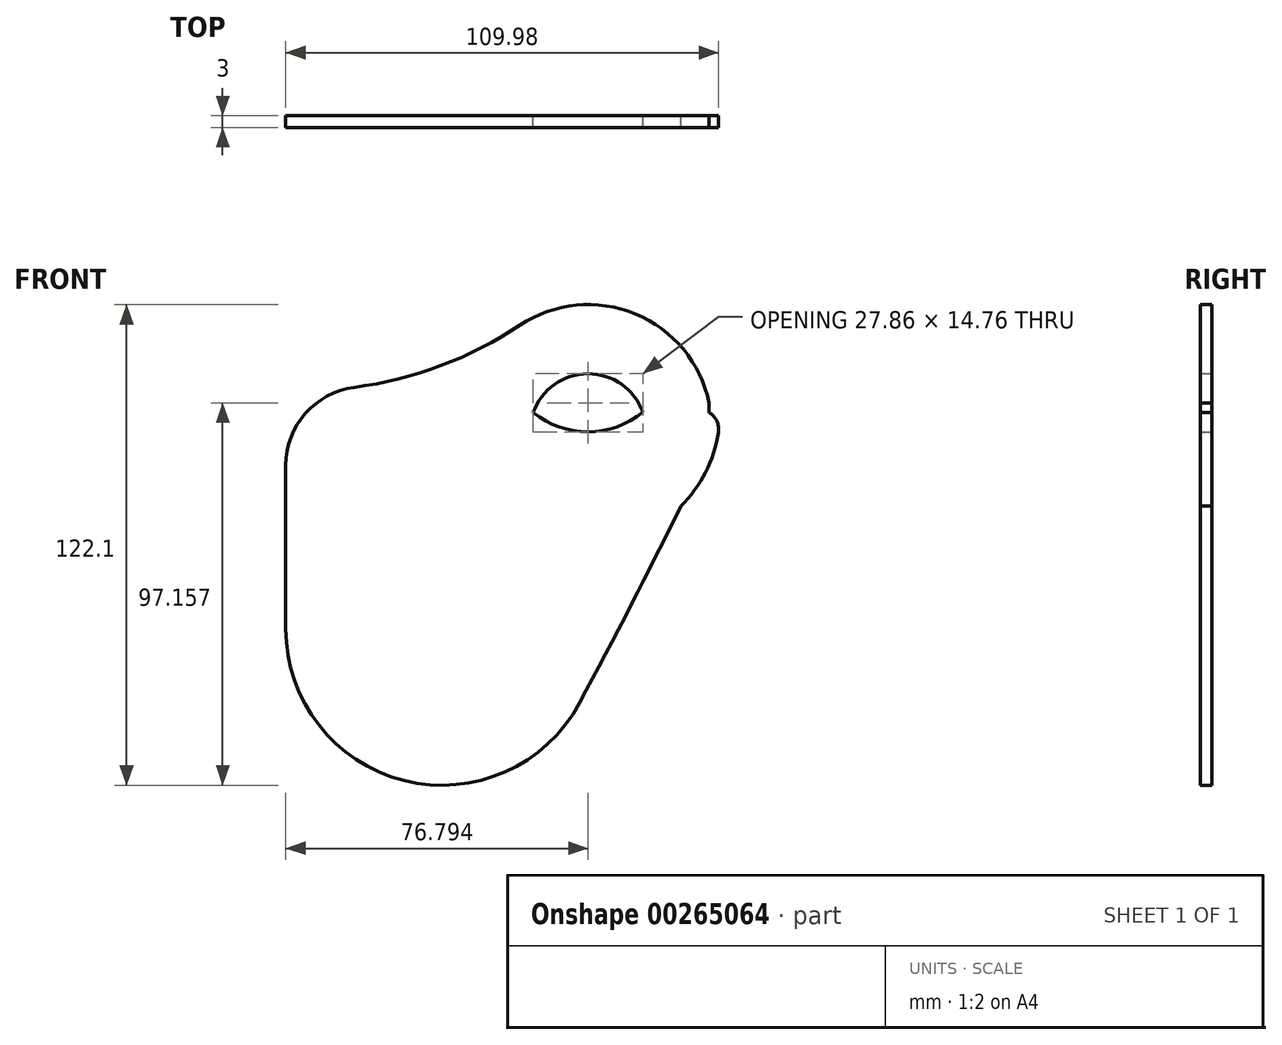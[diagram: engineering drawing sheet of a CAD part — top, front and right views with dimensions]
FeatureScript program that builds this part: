
annotation { "Feature Type Name" : "Feature", "Feature Type Description" : "" }
export const myFeature = defineFeature(function(context is Context, id is Id, definition is map)
    precondition{}
    {
        {
            var Q0;
            Q0=qCreatedBy(makeId("Front.planeOp"),FACE);
            var sketch = newSketch(context, id + "F0", { "sketchPlane" : qUnion([Q0])});
            skArc(sketch, "E0", {"start": v(-23.37, 71.6) * mm, "mid": v(-42.37, 87.06) * mm, "end": v(-61.37, 71.6) * mm});
            skPoint(sketch, "E1", {"position": v(-25.38, 77.03) * mm});
            skArc(sketch, "E2", {"start": v(-56.37, 71.6) * mm, "mid": v(-42.42, 66.69) * mm, "end": v(-28.5, 71.7) * mm});
            skArc(sketch, "E3", {"start": v(-28.5, 71.7) * mm, "mid": v(-42.48, 81.45) * mm, "end": v(-56.37, 71.6) * mm});
            skPoint(sketch, "E4", {"position": v(-42.37, 87.06) * mm});
            skPoint(sketch, "E5", {"position": v(-30.58, 56.7) * mm});
            skArc(sketch, "E6", {"start": v(-61.37, 71.6) * mm, "mid": v(-42.37, 52.6) * mm, "end": v(-23.37, 71.6) * mm});
            skPoint(sketch, "E7", {"position": v(-42.37, 52.6) * mm});
            skPoint(sketch, "E8", {"position": v(-61.37, 71.6) * mm});
            skPoint(sketch, "E9", {"position": v(-56.96, 80.44) * mm});
            skPoint(sketch, "E10", {"position": v(-68.92, 94.73) * mm});
            skArc(sketch, "E11", {"start": v(-57.31, 4.66) * mm, "mid": v(-44.8, 28.42) * mm, "end": v(-32.7, 52.4) * mm});
            skPoint(sketch, "E12", {"position": v(-29.37, 71.03) * mm});
            skLineSegment(sketch, "E13", {"start": v(-104.78, 66.2) * mm, "end": v(-104.78, 16.6) * mm});
            skArc(sketch, "E14", {"start": v(-104.78, 16.6) * mm, "mid": v(-85.7, -7.88) * mm, "end": v(-57.31, 4.66) * mm});
            skPoint(sketch, "E15", {"position": v(-85.15, 92.16) * mm});
            skPoint(sketch, "E16", {"position": v(-79.37, -8.64) * mm});
            skPoint(sketch, "E17.endSnap0", {"position": v(-42.4, 59.62) * mm});
            skLineSegment(sketch, "E18", {"start": v(-28.5, 71.7) * mm, "end": v(-23.37, 71.6) * mm});
            skLineSegment(sketch, "E19", {"start": v(-61.37, 71.6) * mm, "end": v(-56.37, 71.6) * mm});
            skLineSegment(sketch, "E20", {"start": v(-42.42, 66.69) * mm, "end": v(-42.42, 66.65) * mm});
            skPoint(sketch, "E21", {"position": v(-24.15, 66.23) * mm});
            skPoint(sketch, "E22", {"position": v(-59.84, 76.1) * mm});
            skPoint(sketch, "E23", {"position": v(-60.59, 66.2) * mm});
            skLineSegment(sketch, "E24.bottom", {"start": v(-26.7, 79.1) * mm, "end": v(-27.38, 79.1) * mm});
            skPoint(sketch, "E25", {"position": v(-108.66, 79.1) * mm});
            skLineSegment(sketch, "E26.top", {"start": v(-109.39, 67.1) * mm, "end": v(-109.78, 67.1) * mm});
            skLineSegment(sketch, "E27.left", {"start": v(-39.95, 71.09) * mm, "end": v(-39.95, 71.09) * mm});
            skLineSegment(sketch, "E27.right", {"start": v(-42.68, 71.09) * mm, "end": v(-42.68, 71.09) * mm});
            skLineSegment(sketch, "E28.top", {"start": v(-63.18, 66.2) * mm, "end": v(-68.59, 66.2) * mm});
            skPoint(sketch, "E29.orphan", {"position": v(-114.78, 67.1) * mm});
            skPoint(sketch, "E30.top.start.orphan", {"position": v(-109.78, 64.1) * mm});
            skPoint(sketch, "E17.end.orphan", {"position": v(-42.4, 81.45) * mm});
            skLineSegment(sketch, "E31.trimOffspring", {"start": v(-109.78, 54.6) * mm, "end": v(-109.78, 51.6) * mm});
            skPoint(sketch, "E32.top.end.orphan", {"position": v(-106.78, 10.37) * mm});
            skPoint(sketch, "E32.left.start.orphan", {"position": v(-109.78, 35.77) * mm});
            skPoint(sketch, "E27.bottom.start.orphan", {"position": v(-48.6, 10.37) * mm});
            skPoint(sketch, "E27.top.end.orphan", {"position": v(-51.33, 10.37) * mm});
            skPoint(sketch, "E33.start.orphan", {"position": v(-38.82, 35.77) * mm});
            skArc(sketch, "E34.0", {"start": v(-55.1, 3.47) * mm, "mid": v(-41.61, 29.17) * mm, "end": v(-28.58, 55.1) * mm});
            skArc(sketch, "E34.1", {"start": v(-107.28, 16.6) * mm, "mid": v(-86.31, -10.3) * mm, "end": v(-55.1, 3.47) * mm});
            skLineSegment(sketch, "E34.2", {"start": v(-107.28, 66.2) * mm, "end": v(-107.28, 16.6) * mm});
            skLineSegment(sketch, "E35", {"start": v(-20.87, 71.6) * mm, "end": v(-23.37, 71.6) * mm});
            skLineSegment(sketch, "E36", {"start": v(-68.59, 66.2) * mm, "end": v(-107.28, 66.2) * mm});
            skArc(sketch, "E37.0", {"start": v(-63.87, 71.6) * mm, "mid": v(-42.37, 50.1) * mm, "end": v(-20.87, 71.6) * mm});
            skLineSegment(sketch, "E38", {"start": v(-61.37, 71.6) * mm, "end": v(-63.87, 71.6) * mm});
            skPoint(sketch, "E39", {"position": v(-80.6, -11.12) * mm});
            skPoint(sketch, "E40", {"position": v(-80.6, 66.2) * mm});
            skArc(sketch, "E41.0", {"start": v(-44.59, -2.18) * mm, "mid": v(-31.5, 22.7) * mm, "end": v(-18.85, 47.82) * mm});
            skArc(sketch, "E41.1", {"start": v(-119.23, 16.6) * mm, "mid": v(-89.23, -21.89) * mm, "end": v(-44.59, -2.18) * mm});
            skLineSegment(sketch, "E41.2", {"start": v(-119.23, 66.2) * mm, "end": v(-119.23, 16.6) * mm});
            skArc(sketch, "E42.0", {"start": v(-11.67, 74.02) * mm, "mid": v(-40.22, 98.93) * mm, "end": v(-71.9, 78.15) * mm});
            skLineSegment(sketch, "E43.0", {"start": v(-71.9, 78.15) * mm, "end": v(-107.28, 78.15) * mm});
            skArc(sketch, "E44.0", {"start": v(-18.85, 47.82) * mm, "mid": v(-11.5, 58.71) * mm, "end": v(-8.93, 71.6) * mm});
            skLineSegment(sketch, "E45", {"start": v(-119.23, 66.2) * mm, "end": v(-119.23, 78.15) * mm});
            skLineSegment(sketch, "E46", {"start": v(-107.28, 78.15) * mm, "end": v(-119.23, 78.15) * mm});
            skLineSegment(sketch, "E47", {"start": v(-8.93, 71.6) * mm, "end": v(-11.67, 71.6) * mm});
            skLineSegment(sketch, "E48", {"start": v(-11.67, 71.6) * mm, "end": v(-11.67, 74.02) * mm});
            skPoint(sketch, "E49.orphan", {"position": v(-73.06, 74.02) * mm});
            skPoint(sketch, "E50.end.orphan", {"position": v(-73.06, 71.6) * mm});
            skPoint(sketch, "E51.orphan", {"position": v(-119.23, 79.1) * mm});
            skLineSegment(sketch, "E52", {"start": v(-8.93, 71.6) * mm, "end": v(-14.38, 81.77) * mm});
            skSolve(sketch);
        }
        {
            var Q0;
            Q0=makeQuery(id+"F0.imprint","IMPRINT",FACE,{"disambiguationData":[TD([[makeQuery(id+"F0.imprint","IMPRINT",EDGE,{"derivedFrom":sQuery(id+"F0.wireOp",EDGE,"E3")}),-1.0]])]});
            var Q1;
            {var subQ2=sQuery(id+"F0.wireOp",EDGE,"E11");Q1=makeQuery(id+"F0.imprint","IMPRINT",FACE,{"disambiguationData":[TD([[makeQuery(id+"F0.imprint","IMPRINT",EDGE,{"derivedFrom":subQ2}),-1.0]])]});}
            var Q2;
            Q2=makeQuery(id+"F0.imprint","IMPRINT",FACE,{"disambiguationData":[TD([[makeQuery(id+"F0.imprint","IMPRINT",EDGE,{"derivedFrom":sQuery(id+"F0.wireOp",EDGE,"E6")}),1.0]])]});
            var Q3;
            {var subQ1=sQuery(id+"F0.wireOp",EDGE,"E11");Q3=makeQuery(id+"F0.imprint","IMPRINT",FACE,{"disambiguationData":[TD([[makeQuery(id+"F0.imprint","IMPRINT",EDGE,{"derivedFrom":subQ1}),1.0]])]});}
            var Q4;
            {var subQ0=sQuery(id+"F0.wireOp",EDGE,"E3");Q4=makeQuery(id+"F0.imprint","IMPRINT",FACE,{"disambiguationData":[TD([[makeQuery(id+"F0.imprint","IMPRINT",EDGE,{"derivedFrom":subQ0}),1.0]])]});}
            var Q5;
            Q5=makeQuery(id+"F0.imprint","IMPRINT",FACE,{"disambiguationData":[TD([[makeQuery(id+"F0.imprint","IMPRINT",EDGE,{"derivedFrom":sQuery(id+"F0.wireOp",EDGE,"E6")}),-1.0]])]});
            var Q6;
            {var subQ1=sQuery(id+"F0.wireOp",EDGE,"E28.top");Q6=makeQuery(id+"F0.imprint","IMPRINT",FACE,{"disambiguationData":[TD([[makeQuery(id+"F0.imprint","IMPRINT",EDGE,{"derivedFrom":subQ1}),-1.0]])]});}
            extrude(context, id + "F1", {"entities" : qUnion([Q0, Q1, Q2, Q3, Q4, Q5, Q6]), "depth" : 3 * mm, "offsetDistance" : 25 * mm});
        }
        {
            var Q0;
            {var subQ0=sQuery(id+"F0.wireOp",EDGE,"E3");Q0=makeQuery(id+"F0.imprint","IMPRINT",FACE,{"disambiguationData":[TD([[makeQuery(id+"F0.imprint","IMPRINT",EDGE,{"derivedFrom":subQ0}),1.0]])]});}
            extrude(context, id + "F2", {"entities" : qUnion([Q0]), "operationType" : NewBodyOperationType.REMOVE, "depth" : 25 * mm, "offsetDistance" : 25 * mm});
        }
        {
            var Q0;
            Q0=makeQuery(id+"F1.opExtrude","SWEPT_EDGE",EDGE,{"disambiguationData":[OSD([sQuery(id+"F0.wireOp",EDGE,"E45"),sQuery(id+"F0.wireOp",EDGE,"E46")])]});
            fillet(context, id + "F3", {"entities" : qUnion([Q0]), "radius" : 20 * mm, "tangentPropagation" : true, "allowEdgeOverflow" : false});
        }
        {
            var Q0;
            Q0=makeQuery(id+"F1.opExtrude","SWEPT_EDGE",EDGE,{"disambiguationData":[OSD([sQuery(id+"F0.wireOp",EDGE,"E42.0"),sQuery(id+"F0.wireOp",EDGE,"E43.0")])]});
            fillet(context, id + "F4", {"entities" : qUnion([Q0]), "radius" : 100 * mm, "tangentPropagation" : true, "allowEdgeOverflow" : false});
        }
        {
            var Q0;
            Q0=makeQuery(id+"F1.opExtrude","SWEPT_EDGE",EDGE,{"disambiguationData":[OSD([sQuery(id+"F0.wireOp",EDGE,"E44.0"),sQuery(id+"F0.wireOp",EDGE,"E47")])]});
            fillet(context, id + "F5", {"entities" : qUnion([Q0]), "radius" : 5 * mm, "tangentPropagation" : true, "allowEdgeOverflow" : false});
        }
    });
